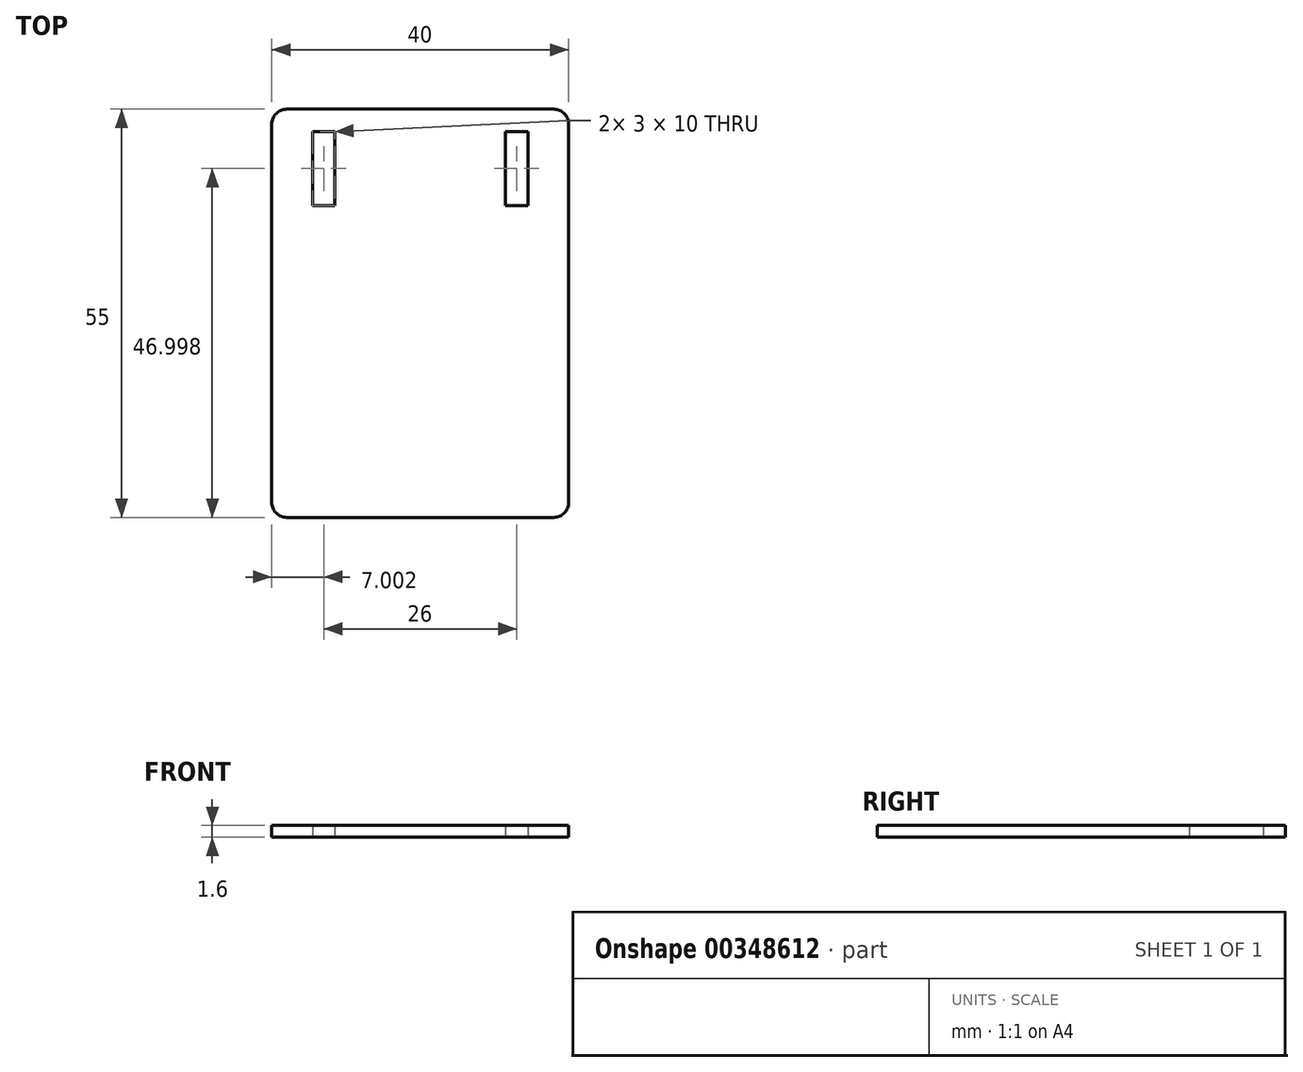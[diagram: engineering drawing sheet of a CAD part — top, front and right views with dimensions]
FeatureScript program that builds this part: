
annotation { "Feature Type Name" : "Feature", "Feature Type Description" : "" }
export const myFeature = defineFeature(function(context is Context, id is Id, definition is map)
    precondition{}
    {
        {
            var Q0;
            Q0=qCreatedBy(makeId("Top.planeOp"),FACE);
            var sketch = newSketch(context, id + "F0", { "sketchPlane" : qUnion([Q0])});
            skLineSegment(sketch, "E0.bottom", {"start": v(-12.96, 25.26) * mm, "end": v(23.04, 25.26) * mm});
            skLineSegment(sketch, "E0.top", {"start": v(-12.96, -29.74) * mm, "end": v(23.04, -29.74) * mm});
            skLineSegment(sketch, "E0.left", {"start": v(-14.96, 23.26) * mm, "end": v(-14.96, -27.74) * mm});
            skLineSegment(sketch, "E0.right", {"start": v(25.04, 23.26) * mm, "end": v(25.04, -27.74) * mm});
            skLineSegment(sketch, "E1.bottom", {"start": v(-9.46, 22.26) * mm, "end": v(-6.46, 22.26) * mm});
            skLineSegment(sketch, "E1.top", {"start": v(-9.46, 12.26) * mm, "end": v(-6.46, 12.26) * mm});
            skLineSegment(sketch, "E1.left", {"start": v(-9.46, 22.26) * mm, "end": v(-9.46, 12.26) * mm});
            skLineSegment(sketch, "E1.right", {"start": v(-6.46, 22.26) * mm, "end": v(-6.46, 12.26) * mm});
            skLineSegment(sketch, "E2.bottom", {"start": v(16.54, 22.26) * mm, "end": v(19.54, 22.26) * mm});
            skLineSegment(sketch, "E2.top", {"start": v(16.54, 12.26) * mm, "end": v(19.54, 12.26) * mm});
            skLineSegment(sketch, "E2.left", {"start": v(16.54, 22.26) * mm, "end": v(16.54, 12.26) * mm});
            skLineSegment(sketch, "E2.right", {"start": v(19.54, 22.26) * mm, "end": v(19.54, 12.26) * mm});
            skPoint(sketch, "E3.visualSharp", {"position": v(-14.96, -29.74) * mm});
            skArc(sketch, "E3.filletArc", {"start": v(-14.96, -27.74) * mm, "mid": v(-14.37, -29.16) * mm, "end": v(-12.96, -29.74) * mm});
            skPoint(sketch, "E4.visualSharp", {"position": v(25.04, -29.74) * mm});
            skArc(sketch, "E4.filletArc", {"start": v(23.04, -29.74) * mm, "mid": v(24.46, -29.16) * mm, "end": v(25.04, -27.74) * mm});
            skPoint(sketch, "E5.visualSharp", {"position": v(-14.96, 25.26) * mm});
            skArc(sketch, "E5.filletArc", {"start": v(-12.96, 25.26) * mm, "mid": v(-14.37, 24.67) * mm, "end": v(-14.96, 23.26) * mm});
            skPoint(sketch, "E6.visualSharp", {"position": v(25.04, 25.26) * mm});
            skArc(sketch, "E6.filletArc", {"start": v(25.04, 23.26) * mm, "mid": v(24.46, 24.67) * mm, "end": v(23.04, 25.26) * mm});
            skSolve(sketch);
        }
        {
            var Q0;
            Q0 = qSketchRegion(id + "F0", true);
            extrude(context, id + "F1", {"entities" : qUnion([Q0]), "depth" : 1.6 * mm});
        }
    });
